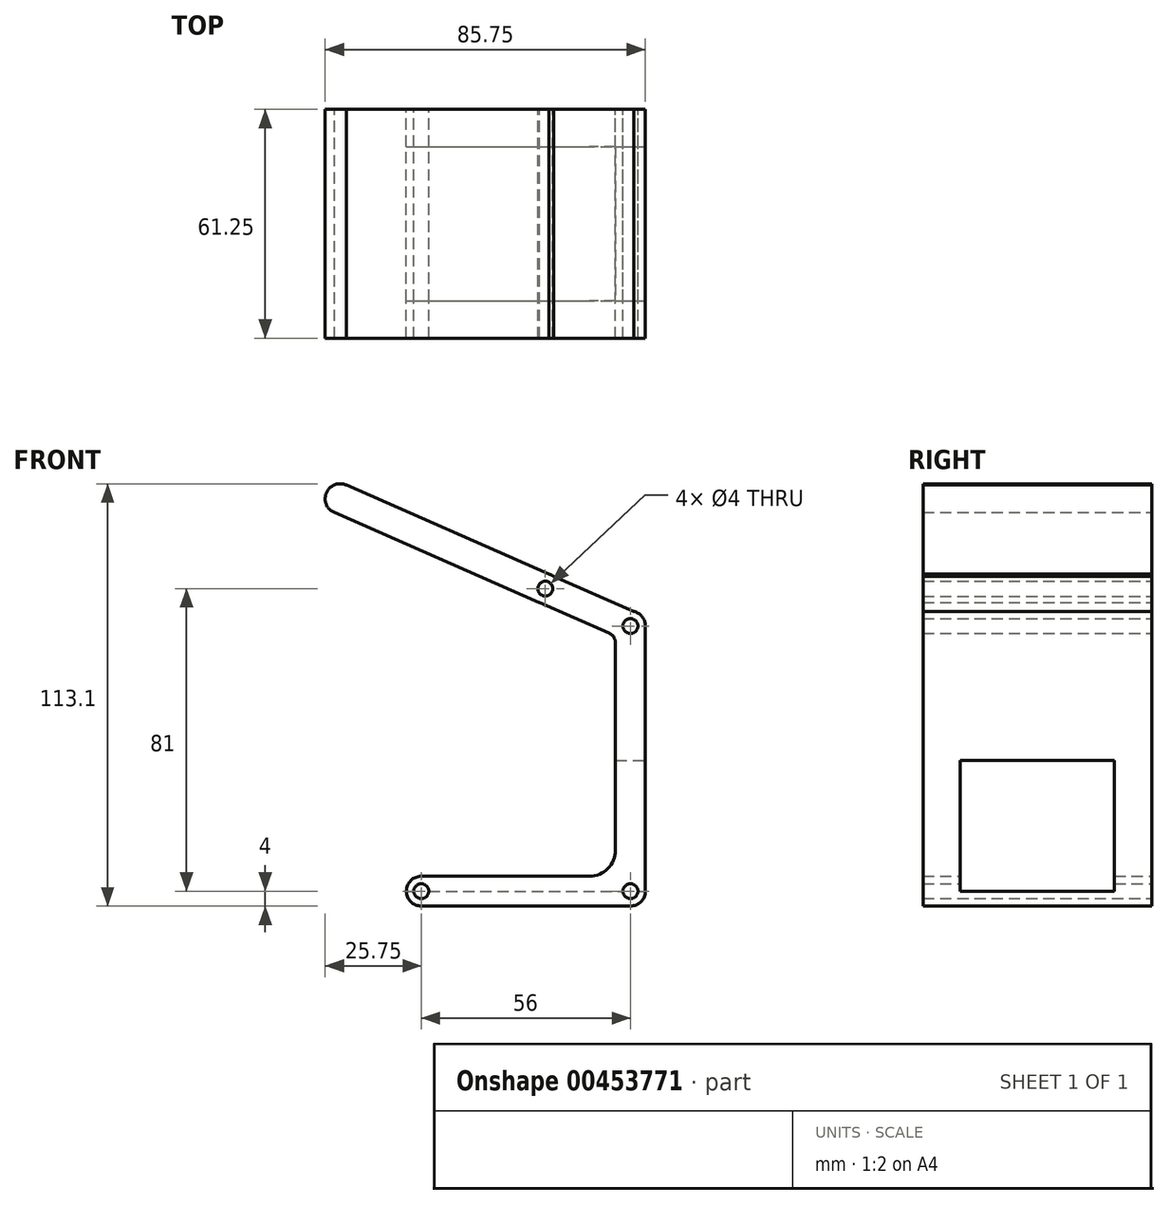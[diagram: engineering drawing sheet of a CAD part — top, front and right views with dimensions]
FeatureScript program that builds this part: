
annotation { "Feature Type Name" : "Feature", "Feature Type Description" : "" }
export const myFeature = defineFeature(function(context is Context, id is Id, definition is map)
    precondition{}
    {
        {
            var Q0;
            Q0=qCreatedBy(makeId("Front.planeOp"),FACE);
            var sketch = newSketch(context, id + "F0", { "sketchPlane" : qUnion([Q0])});
            skCircle(sketch, "E0", {"center": v(0, 0) * mm, "radius": 2 * mm});
            skCircle(sketch, "E1", {"center": v(0, 71) * mm, "radius": 2 * mm});
            skArc(sketch, "E2", {"start": v(4, 71) * mm, "mid": v(3.11, 73.51) * mm, "end": v(0.85, 74.9) * mm});
            skArc(sketch, "E3", {"start": v(0, -4) * mm, "mid": v(2.83, -2.83) * mm, "end": v(4, 0) * mm});
            skCircle(sketch, "E4", {"center": v(-56, 0) * mm, "radius": 2 * mm});
            skArc(sketch, "E5", {"start": v(-56, 4) * mm, "mid": v(-60, 0) * mm, "end": v(-56, -4) * mm});
            skCircle(sketch, "E6", {"center": v(-22.8, 81) * mm, "radius": 2 * mm});
            skArc(sketch, "E7", {"start": v(-24.45, 77.36) * mm, "mid": v(-24.4, 77.34) * mm, "end": v(-24.36, 77.32) * mm});
            skLineSegment(sketch, "E8", {"start": v(0, 71) * mm, "end": v(-1.83, 71.8) * mm});
            skArc(sketch, "E9", {"start": v(-76.1, 108.74) * mm, "mid": v(-81.42, 106.68) * mm, "end": v(-79.27, 101.4) * mm});
            skLineSegment(sketch, "E10", {"start": v(-56, -4) * mm, "end": v(0, -4) * mm});
            skLineSegment(sketch, "E11", {"start": v(-11, 4) * mm, "end": v(-56, 4) * mm});
            skLineSegment(sketch, "E12", {"start": v(4, 71) * mm, "end": v(4, 0) * mm});
            skLineSegment(sketch, "E13", {"start": v(-4, 11) * mm, "end": v(-4, 66.43) * mm});
            skLineSegment(sketch, "E14", {"start": v(-76.1, 108.74) * mm, "end": v(2.3, 74.27) * mm});
            skLineSegment(sketch, "E15", {"start": v(-79.27, 101.4) * mm, "end": v(-5.8, 69.17) * mm});
            skArc(sketch, "E16.trimOffspring", {"start": v(-20.6, 84.34) * mm, "mid": v(-21.19, 84.66) * mm, "end": v(-21.83, 84.88) * mm});
            skPoint(sketch, "E17.orphan", {"position": v(0, 4) * mm});
            skPoint(sketch, "E18.orphan", {"position": v(-4, 0) * mm});
            skPoint(sketch, "E19.visualSharp", {"position": v(-4, 4) * mm});
            skArc(sketch, "E19.filletArc", {"start": v(-11, 4) * mm, "mid": v(-6.05, 6.05) * mm, "end": v(-4, 11) * mm});
            skPoint(sketch, "E20.visualSharp", {"position": v(-4, 68.39) * mm});
            skArc(sketch, "E20.filletArc", {"start": v(-4, 66.43) * mm, "mid": v(-4.49, 68.07) * mm, "end": v(-5.8, 69.17) * mm});
            skSolve(sketch);
        }
        {
            var Q0;
            Q0 = qSketchRegion(id + "F0", true);
            extrude(context, id + "F1", {"entities" : qUnion([Q0]), "depth" : 61.25 * mm});
        }
        {
            var Q0;
            Q0=makeQuery(id+"F1.opExtrude","SWEPT_FACE",FACE,{"disambiguationData":[OSD([sQuery(id+"F0.wireOp",EDGE,"E12")])]});
            var sketch = newSketch(context, id + "F2", { "sketchPlane" : qUnion([Q0])});
            skSolve(sketch);
        }
        {
            var Q0;
            {var subQ0=sQuery(id+"F0.wireOp",EDGE,"E12");Q0=makeQuery(id+"F2.imprint","IMPRINT",FACE,{"disambiguationData":[TD([[makeQuery(id+"F2.imprint","IMPRINT",EDGE,{"derivedFrom":makeQuery(id+"F1.opExtrude","CAP_EDGE",EDGE,{"disambiguationData":[OSD([subQ0])],"isStart":true})}),-1.0]])]});}
            var sketch = newSketch(context, id + "F3", { "sketchPlane" : qUnion([Q0])});
            skLineSegment(sketch, "E21.bottom", {"start": v(0, 0) * mm, "end": v(-61.25, 0) * mm});
            skLineSegment(sketch, "E21.top", {"start": v(0, 60) * mm, "end": v(-61.25, 60) * mm});
            skLineSegment(sketch, "E21.left", {"start": v(0, 0) * mm, "end": v(0, 60) * mm});
            skLineSegment(sketch, "E21.right", {"start": v(-61.25, 0) * mm, "end": v(-61.25, 60) * mm});
            skLineSegment(sketch, "E22.bottom", {"start": v(-51.25, 0) * mm, "end": v(-10, 0) * mm});
            skLineSegment(sketch, "E22.top", {"start": v(-51.25, 35) * mm, "end": v(-10, 35) * mm});
            skLineSegment(sketch, "E22.left", {"start": v(-51.25, 0) * mm, "end": v(-51.25, 35) * mm});
            skLineSegment(sketch, "E22.right", {"start": v(-10, 0) * mm, "end": v(-10, 35) * mm});
            skLineSegment(sketch, "E23.left", {"start": v(-51.25, 0) * mm, "end": v(-51.25, 0) * mm});
            skLineSegment(sketch, "E23.right", {"start": v(-10, 0) * mm, "end": v(-10, 0) * mm});
            skLineSegment(sketch, "E24.top", {"start": v(-51.25, -8.56) * mm, "end": v(-10, -8.56) * mm});
            skLineSegment(sketch, "E24.left", {"start": v(-51.25, 0) * mm, "end": v(-51.25, -8.56) * mm});
            skLineSegment(sketch, "E24.right", {"start": v(-10, 0) * mm, "end": v(-10, -8.56) * mm});
            skSolve(sketch);
        }
        {
            var Q0;
            Q0=makeQuery(id+"F3.imprint","IMPRINT",FACE,{"disambiguationData":[TD([[makeQuery(id+"F3.imprint","IMPRINT",EDGE,{"derivedFrom":sQuery(id+"F3.wireOp",EDGE,"E22.bottom")}),-1.0]])]});
            var Q1;
            Q1=makeQuery(id+"F3.imprint","IMPRINT",FACE,{"disambiguationData":[TD([[makeQuery(id+"F3.imprint","IMPRINT",EDGE,{"derivedFrom":sQuery(id+"F3.wireOp",EDGE,"E22.top")}),-1.0]])]});
            extrude(context, id + "F4", {"entities" : qUnion([Q0, Q1]), "operationType" : NewBodyOperationType.REMOVE, "oppositeDirection" : true, "depth" : 65 * mm});
        }
    });
